# Revit family: UNB_Mirror+light_T2909_BIM_FR
name_source: partatom
category: Plumbing Fixtures
revit_build: Autodesk Revit 2017 (Build: 20160225_1515(x64)
units: mm (PartAtom-declared; Revit-internal decimal feet)

## family parameters
Always vertical = No
Cut with Voids When Loaded = No
OmniClass Number = 23.45.05.14.21.11
OmniClass Title = Bath/Shower Units
Part Type = Normal
Room Calculation Point = No
Round Connector Dimension = Use Diameter
Shared = No
Work Plane-Based = No

## types (1)
- T2909AA - MIRROR&LIGHT- 28,6 x 10,2 x (H) 3 cm
    Accessoires = www.idealstandard.be
    Auteur = Ideal Standard
    BOSUseNativeGeometries = 1
    Bim-NomDuProjet = POR_Porcher_Storage_T2909AA
    Caractéristiques = 28,6 x 10,2 x (H) 3 cm - 1x6 W
    CodeBarre = 8014140446743
    ConseilsDInstallation = www.idealstandard.be
    Cost = 0 $
    Couleur = Chrome
    CoûtDeRemplacement = 0
    DateDeCréation = 2018_08_15
    Description = ULYSSE - 28,6 x 10,2 x (H) 3 cm
    Dimensions = 33 x 286 x 102mm
    DuréeGarantie = ans
    DétailGarantie = Constructeur
    Espace = Interne
    Forme = Complexe
    Hauteur = 33 mm
    IfcExportAs = IfcSanitaryTerminalType
    IfcExportType = Storage
    InformationsProduit = www.idealstandard.be
    Largeur = 286 mm
    LienUtile = www.idealstandard.be
    Longueur = 102 mm
    Manufacturer = www.idealstandard.be
    Marque = PORCHER
    Matériel = Glass
    Model = T2909AA
    Nom = POR_Porcher_Storage_T2909AA
    PerformanceAccessibilité = NF
    PoidsNet = 0.16 Kg
    Profondeur = 0 mm  [stored 0 ft]
    Raccordement = Plomberie
    Référence = T2909AA
    Révision = 1
    TypeDImmobilisation = Fixe
    URL = www.idealstandard.be
    Uniclass2015Code = Pr_40_20_76_94
    Uniclass2015Title = Vanity units
    Uniclass2015Version = Products v1.1
    UnitéDeTemps = an
    UrlDuFabricant = www.idealstandard.be
    Version = 1

note: [stored X ft] marks values corroborated as IEEE doubles in the binary element streams (Revit-internal decimal feet)

## geometry (parser evidence)
native form markers: Sweep x2
no freeform markers — native parametric forms only
